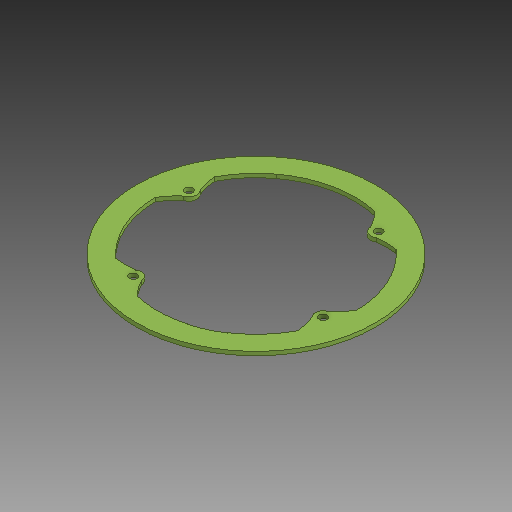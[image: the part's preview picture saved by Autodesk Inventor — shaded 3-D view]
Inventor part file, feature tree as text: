
AUTODESK INVENTOR PART (.ipt)
format: ipt  version: 2020 (Build 240168000, 168)  size: 168,960 bytes
history: native  units: mm
features: other x1, extrude x1, sketch x1
ambient origin geometry x8: Origin, YZ Plane, XZ Plane, XY Plane, X Axis, Y Axis, Z Axis, Center Point
bodies: Body1 (feature_tree)
feature tree (3):
  other  "Твердое тело1"
  extrude  "Выдавливание1"  Depth=1.6mm TaperAngle=0.0deg
  sketch  "Эскиз1"
